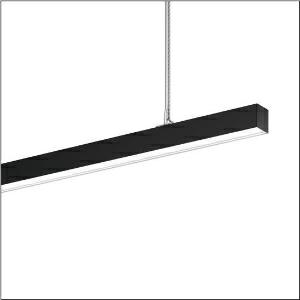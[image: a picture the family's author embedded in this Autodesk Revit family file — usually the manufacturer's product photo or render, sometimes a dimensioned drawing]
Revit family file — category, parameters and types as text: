
# Revit family: silica_r__21_51mx33tat7b_231b
name_source: partatom
category: Lighting Fixtures
units: mm (PartAtom-declared; Revit-internal decimal feet)

## family parameters
Cut with Voids When Loaded = No
Host = Face
Light Source = No
Part Type = Normal
Room Calculation Point = No
Round Connector Dimension = Use Diameter
Shared = No

## types (1)
- --- (1 x LED, 5740 lm, 53.8 W, 6500K)
    Apparent Load = 54 VA
    CIE Flux Codes = 78 96 99 56 100
    Color Rendering = 80
    Color Temperature = 6500K
    Default Elevation = 1800 mm
    Description = Silica® 21, office luminaire, primary optical cover: prismatic diffuser, of PMMA, CAT 2 (L<= 3000cd/m²), light emission: direct/indirect distribution, primary light characteristic: symmetric, installation type: suspended mounting, LED, rated luminous flux: 5.740lm, luminous efficacy: 102lm/W, light colour: 8tw, colour temperature: 2700..6500K, control gear: ECG DALI, with terminal, 3+2-pole, max. 2.5mm², mains connection: 220..240V, AC, 50/60Hz, rated input power: 56.5W, luminaire housing, of aluminium, jet black (RAL 9005), length: 1.204mm, width: 53mm, height: 53mm, protection rating (complete): IP20, insulation class (complete): insulation class I (protective earthing), certification: CE, permissible operating ambient temperature: 0..+35°C, standard: EN 50419, packaging unit: 1 piece
    Height = 53 mm
    Lamp = 1 x LED
    Lamp Light Flux = 5740 lm
    Lamp Power = 53.8 W
    Lamp count = 1
    Length = 1204 mm
    Luminous efficacy = 107 lm/W
    Manufacturer = Siteco
    ModVariant = No
    Model = 51MX33TAT7B
    Mounting Place = Ceiling
    Mounting Type = Pendant
    Number of Poles = 1
    OnlyDefault = Yes
    Power Factor = 1
    Product Name = Silica® 21
    Product group = office luminaire | ceiling pendant
    ProductGroupID = 902
    Protection Class = Protection class I
    Protection Degree = IP 20
    RLX_Detail_Level = 1
    RLX_Emergency_Light_Flux = 0 lm
    RLX_Emergency_Type = 0
    RLX_Emergency_Type_DB = No
    RlxData = <blob elided: 22893 chars, md5=17f8fc38>
    Socket = socket
    Standby Power = 0 W
    System Light Flux = 5740 lm
    System Power = 54 W
    Type Comments = individual setting
    Type Image = l_1313646.jpg
    URL = http://relux.com
    VarID = @adj_089133
    Voltage = 0 V
    Weight = 0.00 kg
    Width = 53 mm

## geometry (parser evidence)
native form markers: Blend x4, Sweep x14
no freeform markers — native parametric forms only
